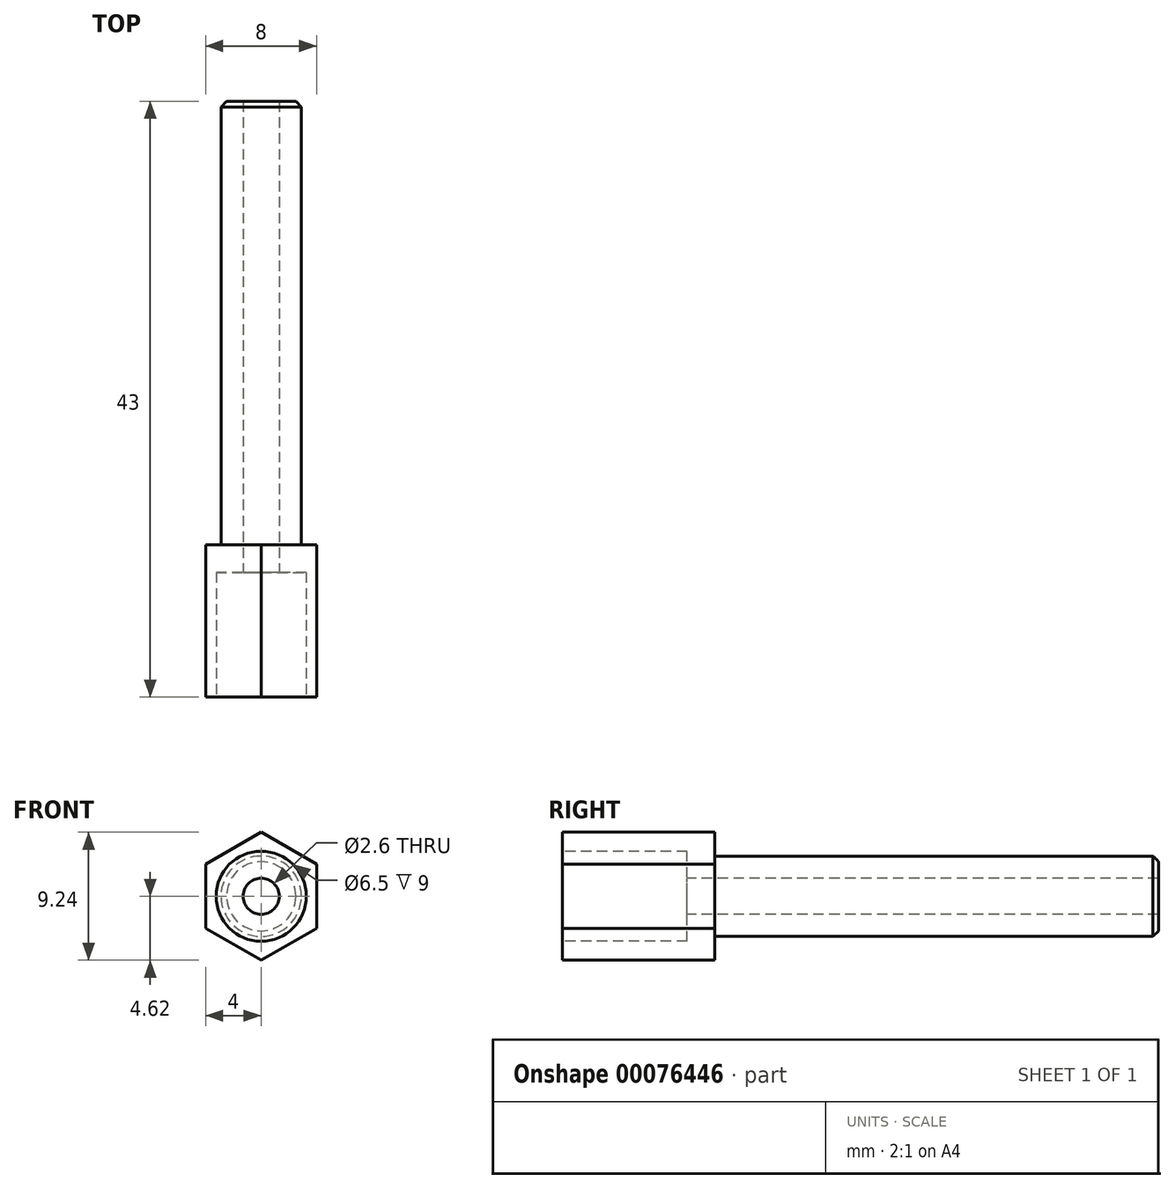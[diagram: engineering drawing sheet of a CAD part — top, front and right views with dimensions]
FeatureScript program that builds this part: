
annotation { "Feature Type Name" : "Feature", "Feature Type Description" : "" }
export const myFeature = defineFeature(function(context is Context, id is Id, definition is map)
    precondition{}
    {
        {
            var Q0;
            Q0=qCreatedBy(makeId("Front.planeOp"),FACE);
            var sketch = newSketch(context, id + "F0", { "sketchPlane" : qUnion([Q0])});
            skCircle(sketch, "E0.cCircle", {"center": v(0, 0) * mm, "radius": 4 * mm, "construction": true});
            skLineSegment(sketch, "E0.0", {"start": v(0, 4.62) * mm, "end": v(4, 2.3) * mm});
            skLineSegment(sketch, "E0.1", {"start": v(4, 2.3) * mm, "end": v(4, -2.3) * mm});
            skLineSegment(sketch, "E0.2", {"start": v(4, -2.3) * mm, "end": v(0, -4.62) * mm});
            skLineSegment(sketch, "E0.3", {"start": v(0, -4.62) * mm, "end": v(-4, -2.3) * mm});
            skLineSegment(sketch, "E0.4", {"start": v(-4, -2.3) * mm, "end": v(-4, 2.3) * mm});
            skLineSegment(sketch, "E0.5", {"start": v(-4, 2.3) * mm, "end": v(0, 4.62) * mm});
            skPoint(sketch, "E0.0.midPoint", {"position": v(2, 3.46) * mm});
            skLineSegment(sketch, "E1", {"start": v(0, 5.7) * mm, "end": v(0, -5.92) * mm, "construction": true});
            skSolve(sketch);
        }
        {
            var Q0;
            Q0=makeQuery(id+"F0.imprint","IMPRINT",FACE,{"disambiguationData":[TD([[makeQuery(id+"F0.imprint","IMPRINT",EDGE,{"derivedFrom":sQuery(id+"F0.wireOp",EDGE,"E0.0")}),-1.0]])]});
            extrude(context, id + "F1", {"entities" : qUnion([Q0]), "oppositeDirection" : true, "depth" : 11 * mm});
        }
        {
            var Q0;
            Q0=makeQuery(id+"F1.opExtrude","CAP_FACE",FACE,{"disambiguationData":[OSD([sQuery(id+"F0.wireOp",EDGE,"E0.0"),sQuery(id+"F0.wireOp",EDGE,"E0.1"),sQuery(id+"F0.wireOp",EDGE,"E0.2"),sQuery(id+"F0.wireOp",EDGE,"E0.3"),sQuery(id+"F0.wireOp",EDGE,"E0.4"),sQuery(id+"F0.wireOp",EDGE,"E0.5")])],"isStart":false});
            var sketch = newSketch(context, id + "F2", { "sketchPlane" : qUnion([Q0])});
            skCircle(sketch, "E2", {"center": v(0, 0) * mm, "radius": 2.9 * mm});
            skSolve(sketch);
        }
        {
            var Q0;
            Q0=makeQuery(id+"F2.imprint","IMPRINT",FACE,{"disambiguationData":[TD([[makeQuery(id+"F2.imprint","IMPRINT",EDGE,{"derivedFrom":sQuery(id+"F2.wireOp",EDGE,"E2")}),1.0]])]});
            extrude(context, id + "F3", {"entities" : qUnion([Q0]), "operationType" : NewBodyOperationType.ADD, "depth" : 32 * mm});
        }
        {
            var Q0;
            Q0=makeQuery(id+"F1.opExtrude","CAP_FACE",FACE,{"disambiguationData":[OSD([sQuery(id+"F0.wireOp",EDGE,"E0.0"),sQuery(id+"F0.wireOp",EDGE,"E0.1"),sQuery(id+"F0.wireOp",EDGE,"E0.2"),sQuery(id+"F0.wireOp",EDGE,"E0.3"),sQuery(id+"F0.wireOp",EDGE,"E0.4"),sQuery(id+"F0.wireOp",EDGE,"E0.5")])],"isStart":true});
            var sketch = newSketch(context, id + "F4", { "sketchPlane" : qUnion([Q0])});
            skPoint(sketch, "E3", {"position": v(0, 0) * mm});
            skSolve(sketch);
        }
        {
            var Q0;
            Q0=sQuery(id+"F4.wireOp",VERTEX,"E3");
            var Q1;
            Q1=makeQuery(id+"F1.opExtrude","SWEPT_BODY",BODY,{"disambiguationData":[OSD([sQuery(id+"F0.wireOp",EDGE,"E0.0"),sQuery(id+"F0.wireOp",EDGE,"E0.1"),sQuery(id+"F0.wireOp",EDGE,"E0.2"),sQuery(id+"F0.wireOp",EDGE,"E0.3"),sQuery(id+"F0.wireOp",EDGE,"E0.4"),sQuery(id+"F0.wireOp",EDGE,"E0.5")])]});
            hole(context, id + "F5", {"style" : HoleStyle.C_BORE, "endStyle" : HoleEndStyle.THROUGH, "standardTappedOrClearance" : lookupTablePath({ "standard" : "ISO", "size" : "2.6", "type" : "Drilled" }), "standardBlindInLast" : lookupTablePath({ "standard" : "ISO", "size" : "2.6", "type" : "Drilled" }), "holeDiameter" : 2.6 * mm, "cBoreDiameter" : 6.5 * mm, "cBoreDepth" : 9 * mm, "locations" : qUnion([Q0]), "scope" : qUnion([Q1]), "isTappedThrough" : true});
        }
        {
            var Q0;
            Q0=makeQuery(id+"F3.opExtrude","CAP_EDGE",EDGE,{"disambiguationData":[OSD([sQuery(id+"F2.wireOp",EDGE,"E2")])],"isStart":false});
            chamfer(context, id + "F6", {"entities" : qUnion([Q0]), "width" : .4 * mm, "tangentPropagation" : true});
        }
    });
